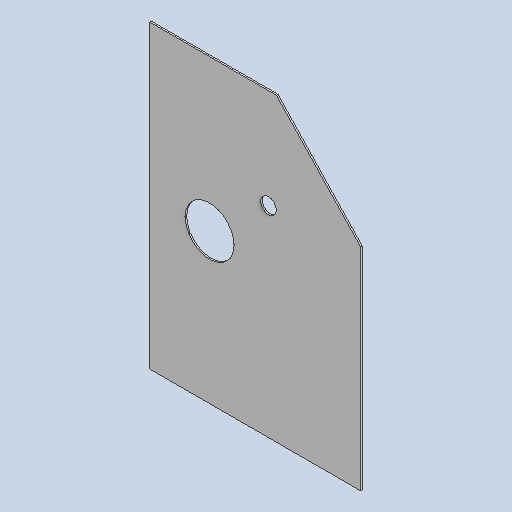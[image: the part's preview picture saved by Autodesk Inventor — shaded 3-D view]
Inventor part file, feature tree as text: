
AUTODESK INVENTOR PART (.ipt)
format: ipt  version: 2025 (Build 290162010, 162A)  size: 191,488 bytes
history: native  units: mm
features: extrude x3, sketch x2, projected_geometry x1, other x1
ambient origin geometry x8: Origin, YZ Plane, XZ Plane, XY Plane, X Axis, Y Axis, Z Axis, Center Point
bodies: Solid1 (feature_tree)
feature tree (7):
  extrude  "Extrusion1"  Depth=1150.0mm
  extrude  "Extrusion3"  Depth=1180.0mm
  extrude  "Extrusion4"  Depth=950.0mm
  sketch  "Sketch3"  dims[d1=840.0mm d3=1150.0mm]
  sketch  "Sketch4"  dims[d11=390.0mm d12=1180.0mm d13=950.0mm d14=76.0mm d15=1910.0mm d16=255.0mm d17=220.0mm d18=400.0mm d19=220.0mm d21=1277.0mm d22=1554.635823mm d23=100.0mm d24=10.0mm d25=0.0mm d33=2140.0mm d34=494.0mm d37=10.0mm d38=0.0mm d45=310.0mm d47=5.0mm d48=80.0mm d49=372.0mm d51=780.0mm d52=1078.0mm d53=1340.0mm d54=0.0mm d55=0.0mm]
  projected_geometry  "Projected Loop1"
  other  "Definition1"
